# Revit family: Lighting-Industriale-GEWISS-ELIA-WL-LED_PLAFONIERA
name_source: partatom
category: Apparecchi per illuminazione
units: mm (PartAtom-declared; Revit-internal decimal feet)

## family parameters
Condiviso = No
Host = Superficie
Punto di calcolo locali = Sì
Quota connettore circolare = Usa diametro
Sorgente d'illuminazione = Sì
Taglio con vuoti quando caricato = No
Tipo di parte = Normale

## types (6) — shared parameters
Angolo inclinazione = 90.00°
Applicazione = Interno
Catalogo = LIGHTING
Catalogo Serie = ELIA WL
Classe isolamento = I
Colore = Bianco
Emetti da lunghezza linea = 610 mm
File diagramma fotometrico = GWS2358PL.IES
Filtro dei colori = 16777215
Garanzia = 5 anni
IDF = 9aa7aeb1-4f1d-4f08-a5fe-9c35326fe2d2
IDT = 94634168-d726-4c19-9922-7cff39855ded
Immagine tipo = ELIA_WL.jpeg
Installazione = Plafone - Parete - Sospensione
LED Life time (L80B50) = L80 B50 (Tq25°) = 54.000h
L_lampada = 1500 mm  [stored 4.92126 ft]
Lampada: = LED
Ottica = Schermo opale
Produttore = GEWISS S.p.A.
Prospetto di default = 1219 mm
Resistenza agli urti = IK08
SEO = Plafone - Parete - Sospensione
Scheda Tecnica = https://www.gewiss.com
Temperatura di colore = 4000K
Temperatura di colore: = 4000K
Tensione = 220-240 VÂ
Tipo lampada = LED
Tipologia = Plafone - Parete - Sospensione
Tipologia sorgente luminosa = LED - Non sostituibile
URL = https://www.gewiss.com
Variazione temperatura colore lampada con luminosità attenuata = <Nessuno>
Versione file RFA = 20.0
Visibilità bidimensionale = 2D frontali : Elia WL 1500
Visibilità frontale = Frontale : 1500

## per-type parameters (varying)
| type | Descrizione | Dimensioni (mm) | Grado di protezione | Lumen output (lm) | Modello | Peso (kg) | Peso (kg): | Potenza di sistema | Temperatura di funzionamento | Temperatura di utilizzo |
| GWS2336P - ELIA WL 1200 OPALE 4000K STAND ALONE | ELIA WL 1200 OPALE 4000K STAND ALONE | 1200 mm | IP66 | 4500 | GWS2336P | 1,7 | 1,7 | 37W | -25 +40 °C | -25 +40 °C |
| GWS2358P - ELIA WL 1500 OPALE 4000K STAND ALONE | ELIA WL 1500 OPALE 4000K STAND ALONE | 1500 mm | IP66 | 5700 | GWS2358P | 2 | 2 | 47W | -25 +40 °C | -25 +40 °C |
| GWS2336PE - ELIA WL 1200 OPALE 4000K EMERGENZA | ELIA WL 1200 OPALE 4000K EMERGENZA | 1200 mm | IP54 | 4500 | GWS2336PE | 2,7 | 2,7 | 42W | 0 +25 °C | 0 +25 °C |
| GWS2358PE - ELIA WL 1500 OPALE 4000K EMERGENZA | ELIA WL 1500 OPALE 4000K EMERGENZA | 1500 mm | IP54 | 5700 | GWS2358PE | 3 | 3 | 52W | 0 +25 °C | 0 +25 °C |
| GWS2336PL - ELIA WL 1200 OPALE 4000K LINEA PASSANTE | ELIA WL 1200 OPALE 4000K LINEA PASSANTE | 1200 mm | IP66 | 4500 | GWS2336PL | 1,7 | 1,7 | 37W | -25 +40 °C | -25 +40 °C |
| GWS2358PL - ELIA WL 1500 OPALE 4000K LINEA PASSANTE | ELIA WL 1500 OPALE 4000K LINEA PASSANTE | 1500 mm | IP66 | 5700 | GWS2358PL | 2 | 2 | 47W | -25 +40 °C | -25 +40 °C |

note: [stored X ft] marks values corroborated as IEEE doubles in the binary element streams (Revit-internal decimal feet)
